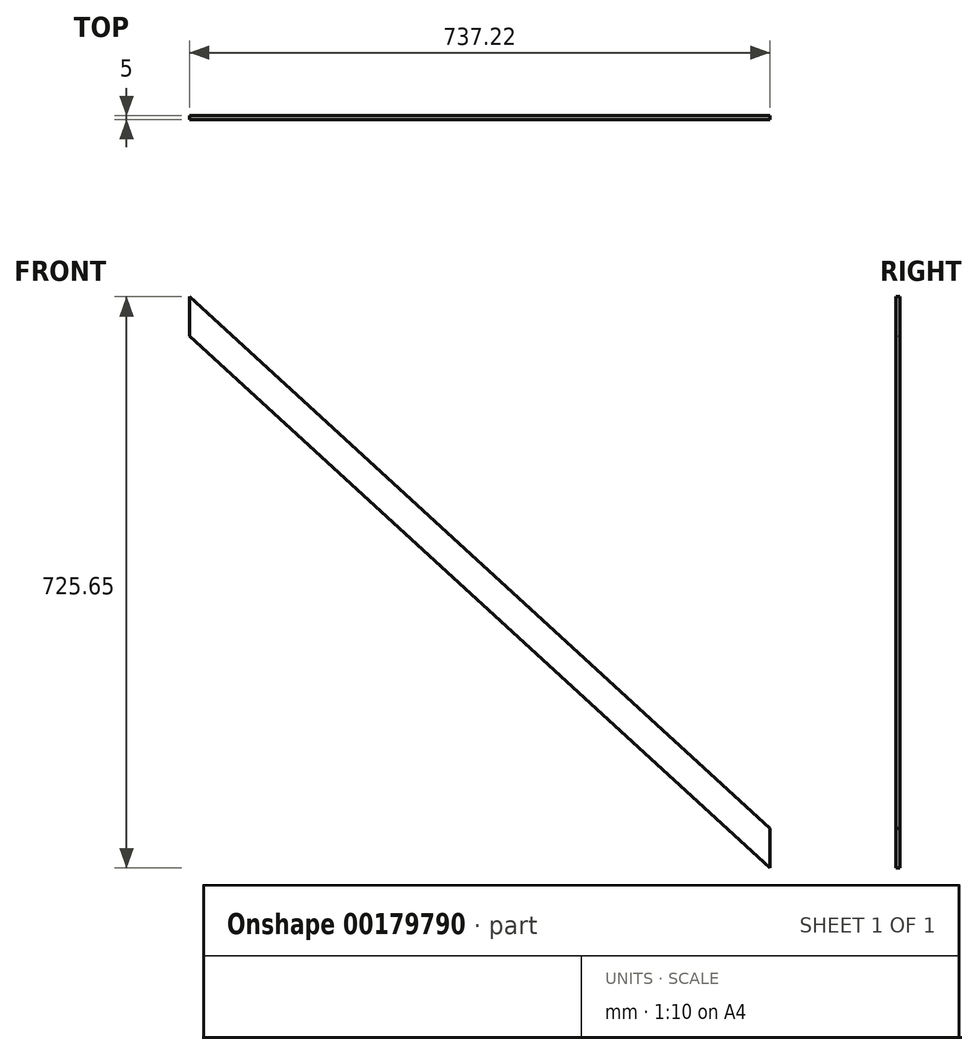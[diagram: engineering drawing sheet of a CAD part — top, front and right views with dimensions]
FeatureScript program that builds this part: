
annotation { "Feature Type Name" : "Feature", "Feature Type Description" : "" }
export const myFeature = defineFeature(function(context is Context, id is Id, definition is map)
    precondition{}
    {
        {
            var Q0;
            Q0=qCreatedBy(makeId("Front.planeOp"),FACE);
            var sketch = newSketch(context, id + "F0", { "sketchPlane" : qUnion([Q0])});
            skLineSegment(sketch, "E0", {"start": v(-57, 81.63) * mm, "end": v(-57, 31.63) * mm});
            skLineSegment(sketch, "E1", {"start": v(-57, 31.63) * mm, "end": v(680.22, -644.02) * mm});
            skLineSegment(sketch, "E2", {"start": v(680.22, -644.02) * mm, "end": v(680.22, -594.02) * mm});
            skLineSegment(sketch, "E3", {"start": v(680.22, -594.02) * mm, "end": v(-57, 81.63) * mm});
            skSolve(sketch);
        }
        {
            var Q0;
            Q0 = qSketchRegion(id + "F0", true);
            extrude(context, id + "F1", {"entities" : qUnion([Q0]), "depth" : 5 * mm});
        }
    });
